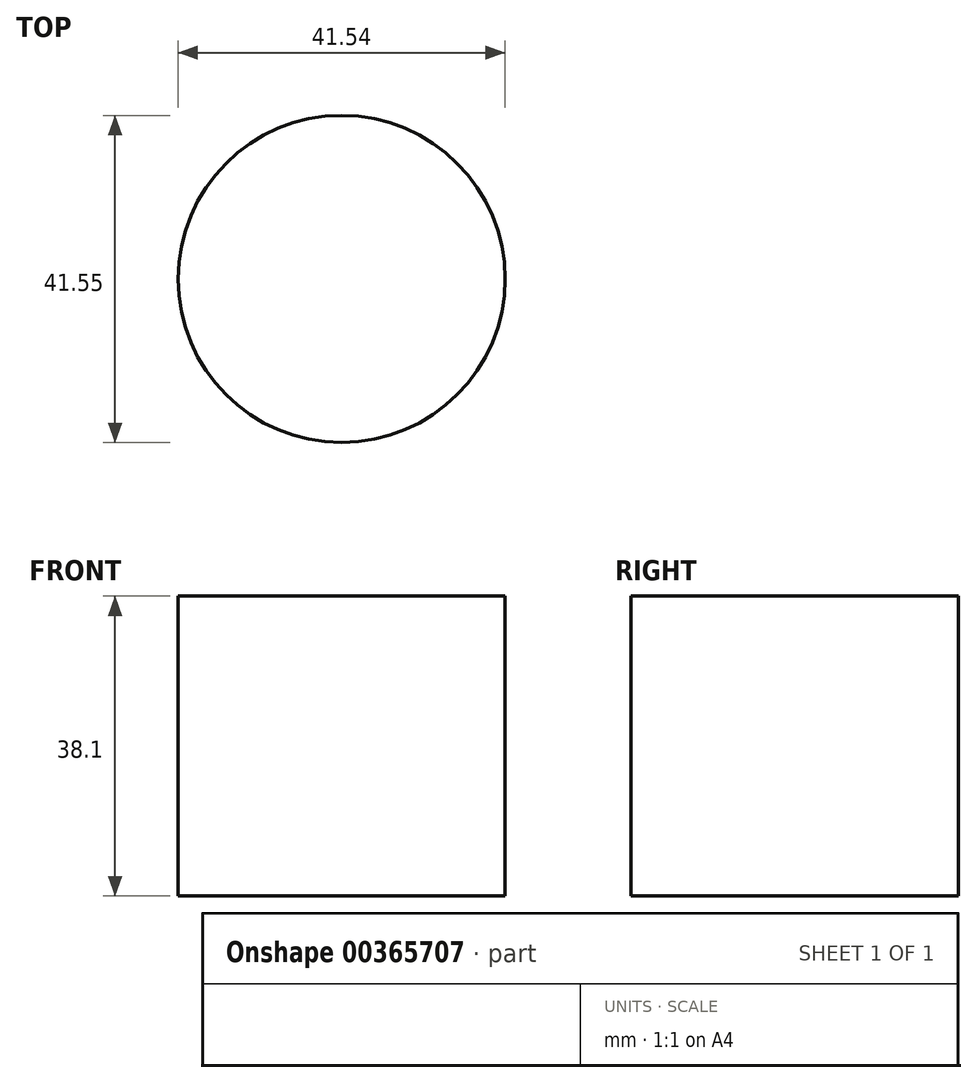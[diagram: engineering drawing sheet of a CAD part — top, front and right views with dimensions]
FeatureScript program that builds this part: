
annotation { "Feature Type Name" : "Feature", "Feature Type Description" : "" }
export const myFeature = defineFeature(function(context is Context, id is Id, definition is map)
    precondition{}
    {
        {
            var Q0;
            Q0=qCreatedBy(makeId("Top.planeOp"),FACE);
            var sketch = newSketch(context, id + "F0", { "sketchPlane" : qUnion([Q0])});
            skLineSegment(sketch, "E0", {"start": v(0, 0) * mm, "end": v(0, -43.68) * mm});
            skCircle(sketch, "E1", {"center": v(0, -43.68) * mm, "radius": 20.77 * mm});
            skSolve(sketch);
        }
        {
            var Q0;
            {var subQ0=sQuery(id+"F0.wireOp",EDGE,"E1");Q0=makeQuery(id+"F0.imprint","IMPRINT",FACE,{"disambiguationData":[TD([[makeQuery(id+"F0.imprint","IMPRINT",EDGE,{"derivedFrom":subQ0}),1.0]])]});}
            extrude(context, id + "F1", {"entities" : qUnion([Q0]), "depth" : 38.1 * mm});
        }
    });
